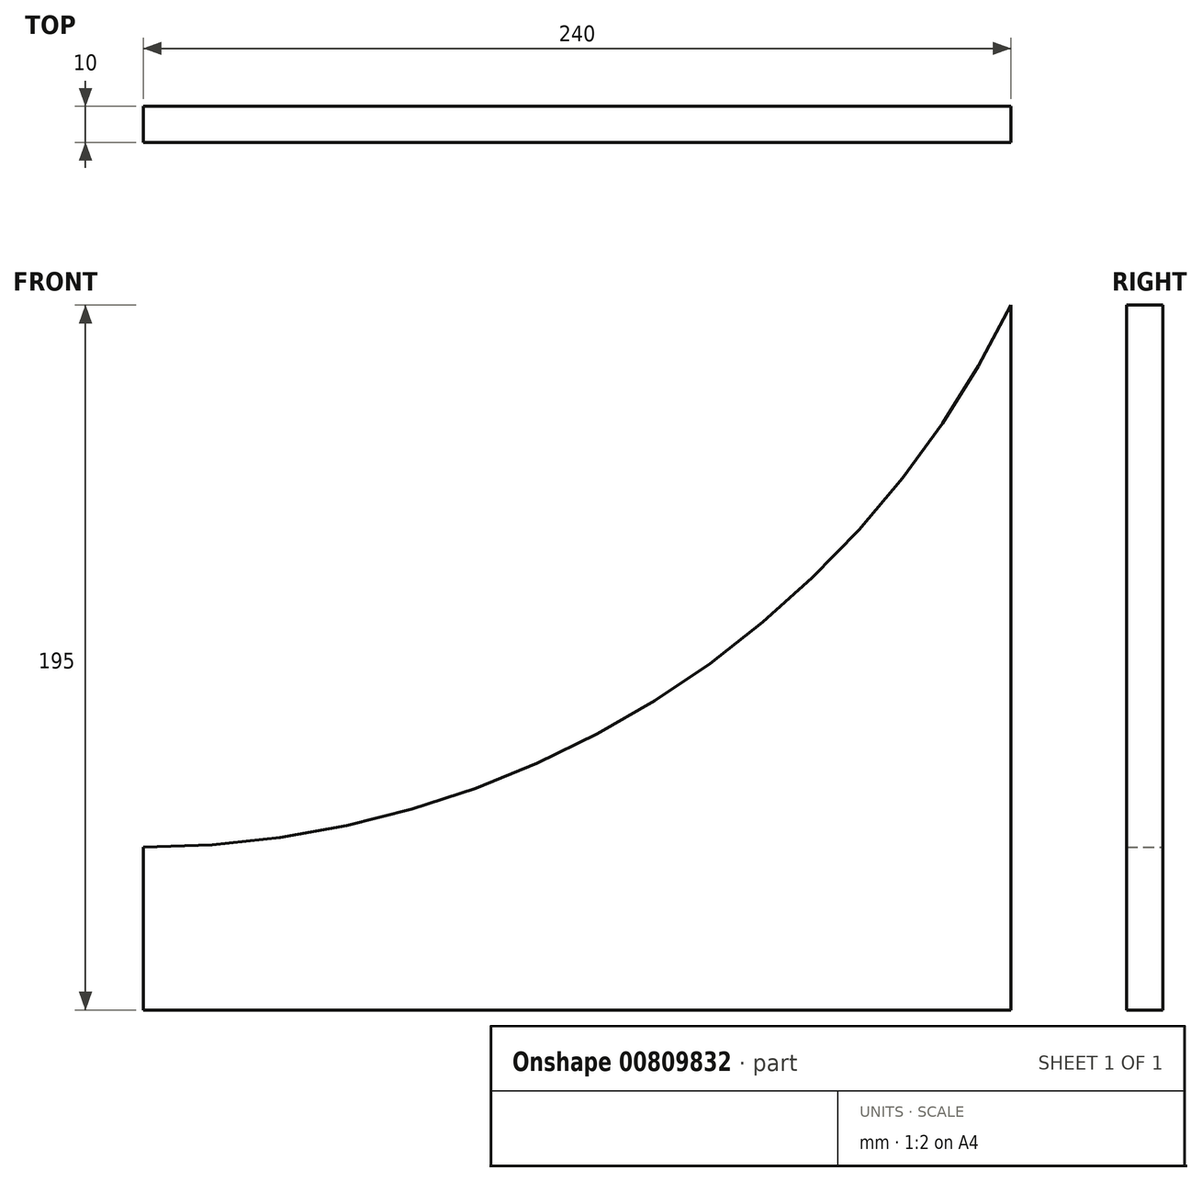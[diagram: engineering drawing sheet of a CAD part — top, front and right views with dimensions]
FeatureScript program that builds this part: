
annotation { "Feature Type Name" : "Feature", "Feature Type Description" : "" }
export const myFeature = defineFeature(function(context is Context, id is Id, definition is map)
    precondition{}
    {
        {
            var Q0;
            Q0=qCreatedBy(makeId("Front.planeOp"),FACE);
            var sketch = newSketch(context, id + "F0", { "sketchPlane" : qUnion([Q0])});
            skLineSegment(sketch, "E0.bottom", {"start": v(120, 22.5) * mm, "end": v(-120, 22.5) * mm});
            skLineSegment(sketch, "E0.top", {"start": v(120, -22.5) * mm, "end": v(-120, -22.5) * mm});
            skLineSegment(sketch, "E0.left", {"start": v(120, 22.5) * mm, "end": v(120, -22.5) * mm});
            skLineSegment(sketch, "E0.right", {"start": v(-120, 22.5) * mm, "end": v(-120, -22.5) * mm});
            skPoint(sketch, "E0.middle", {"position": v(0, 0) * mm});
            skLineSegment(sketch, "E1", {"start": v(120, 22.5) * mm, "end": v(120, 172.5) * mm});
            skArc(sketch, "E2", {"start": v(-120, 22.5) * mm, "mid": v(21.5, 63.08) * mm, "end": v(120, 172.5) * mm});
            skSolve(sketch);
        }
        {
            var Q0;
            Q0=makeQuery(id+"F0.imprint","IMPRINT",FACE,{"disambiguationData":[TD([[makeQuery(id+"F0.imprint","IMPRINT",EDGE,{"derivedFrom":sQuery(id+"F0.wireOp",EDGE,"E0.bottom")}),-1.0]])]});
            var Q1;
            Q1=makeQuery(id+"F0.imprint","IMPRINT",FACE,{"disambiguationData":[TD([[makeQuery(id+"F0.imprint","IMPRINT",EDGE,{"derivedFrom":sQuery(id+"F0.wireOp",EDGE,"E0.bottom")}),1.0]])]});
            extrude(context, id + "F1", {"entities" : qUnion([Q0, Q1]), "depth" : 10 * mm, "offsetDistance" : 25.4 * mm});
        }
    });
